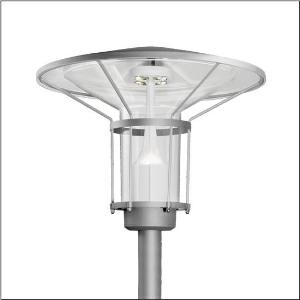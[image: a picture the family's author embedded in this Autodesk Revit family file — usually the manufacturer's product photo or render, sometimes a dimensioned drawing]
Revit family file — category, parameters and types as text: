
# Revit family: laterne_classic_iq___pl1_2s_5xa5245jf14h000022_9e24
name_source: partatom
category: Lighting Fixtures
units: mm (PartAtom-declared; Revit-internal decimal feet)

## family parameters
Cut with Voids When Loaded = No
Host = Face
Light Source = No
Part Type = Normal
Room Calculation Point = No
Round Connector Dimension = Use Diameter
Shared = No

## types (1)
- --- (1 x LED, 2660 lm, 19.3 W, 3000K)
    Apparent Load = 19 VA
    CIE Flux Codes = 21 60 93 97 100
    Color Rendering = 70
    Color Temperature = 3000K
    Default Elevation = 1800 mm
    Description = Lantern Classic iQ, mast luminaire, Module 540 iQ-SR, primary light control with 3 zone facetted reflector, of plastic, silver coated, highly specular, structured, primary optical cover: cover, of PMMA, transparent, light distribution: PL1.2s, light emission: direct distribution, primary light characteristic: symmetric, installation type: post-top, LED, High Power LED, rated luminous flux: 2.660lm, luminous efficacy: 138lm/W, light colour: 730, colour temperature: 3000K, control gear: ECG iQ, control: Street-Remote, Auto-Match, Temp-Guard, Lumen-Switch, Night-Set, Smart-Wire, Light-Fading, Desk-Remote (wireless, voltage-free reading and setting of iQ features in the workshop via application-optimized NFC function/RFID function), optimised constant luminous flux control (CLO 2.0), presetting dimming logarithmic, mains connection: 230..240V, AC, 50/60Hz, connection cable pre-assembled, cable length: 5,5m, wiring characteristics: H07RN-F, start of lifetime: 19W, end of service life: 21W, reduction: 10W, luminaire housing, upper part, of glass-fibre reinforced polyester, coated, Siteco® metallic grey (DB 702S), diameter: 750mm, height: 596mm, spigot size: d x l = 76 x 70mm (post-top) | with reducer (optional accessory) 60 x 70mm, post-top mast mounting element, of diecast aluminium, coated, Siteco® metallic grey (DB 702S), Module 540 iQ-SR, traffic white (RAL 9016), equipment: standard, protection rating (complete): IP65, insulation class (complete): insulation class II (safety insulation), certification: CE, ENEC, VDE, packaging unit: 1 piece

Light Distribution: PL1.2s
    Height = 596 mm
    Lamp = 1 x LED
    Lamp Light Flux = 2660 lm
    Lamp Power = 19.3 W
    Lamp count = 1
    Length = 750 mm
    Luminous efficacy = 138 lm/W
    Manufacturer = Siteco
    ModVariant = No
    Model = 5XA5245JF14H000022
    Number of Poles = 1
    OnlyDefault = Yes
    Power Factor = 1
    Product Name = Laterne Classic iQ | PL1.2s
    Product group = mast luminaire | pylon top
    ProductGroupID = 6100
    Protection Class = Protection class II
    Protection Degree = IP 65
    RLX_Detail_Level = 1
    RLX_Emergency_Light_Flux = 0 lm
    RLX_Emergency_Type = 0
    RLX_Emergency_Type_DB = No
    RlxData = <blob elided: 62725 chars, md5=645842bb>
    Socket = socket
    Standby Power = 0 W
    System Light Flux = 2660 lm
    System Power = 19 W
    Type Comments = factory setting: luminous flux: 100 % | dim-lin: 254 | 403 mA
    Type Image = l_1006052.jpg
    URL = http://relux.com
    VarID = @adj_095235
    Voltage = 0 V
    Weight = 0.00 kg
    Width = 0 mm  [stored 0 ft]

note: [stored X ft] marks values corroborated as IEEE doubles in the binary element streams (Revit-internal decimal feet)

## geometry (parser evidence)
native form markers: Blend x4, Sweep x12
no freeform markers — native parametric forms only
